# Revit family: Haworth_BuzziFalls_Standing_EU_PRELIMINARY
name_source: partatom
category: Furniture
revit_build: Autodesk Revit 2018 (Build: 20170223_1515(x64)
units: mm (PartAtom-declared; Revit-internal decimal feet)

## family parameters
Always vertical = Yes
Cut with Voids When Loaded = No
OmniClass Number = 23.40.70.14.64.21
OmniClass Title = Systems Furniture
Room Calculation Point = No
Shared = No
Work Plane-Based = No

## types (3) — shared parameters
Actual Depth = 2 cm
Actual Height = 204 cm
Assembly Code = E2020200
Description = Haworth - BuzziSpace - BuzziFalls - Standing - Screen
Glide Finish = Haworth _ Paint _ Black BTR-9005
Manufacturer = Haworth
Model = BuzziFalls Standing
Patterns = Plain, Alhambra, Birch, Dots, Grid, Leaves, Orient, Palms, Parrots, Pebbles, Rain, Royal, Tropics
Revision Number = 1
Size = Verify Final Dim. w/ Haworth
URL = https://www.haworth.com
URL - Product = https://www.haworth.com
Warranty = http://www.haworth.com

## per-type parameters (varying)
| type | Actual Width | Add On Screen | Single |
| Single Screen | 84 cm | No | Yes |
| Add on Screen | 84 cm | Yes | No |
| Trio Screen | 256 cm | No | No |

type visibility flags (boolean, named after types; folded from table):
- Single Screen: Yes: (none)
- Add on Screen: Yes: (none)
- Trio Screen: Yes: Trio Screen

## geometry (parser evidence)
native form markers: Sweep x6
no freeform markers — native parametric forms only
